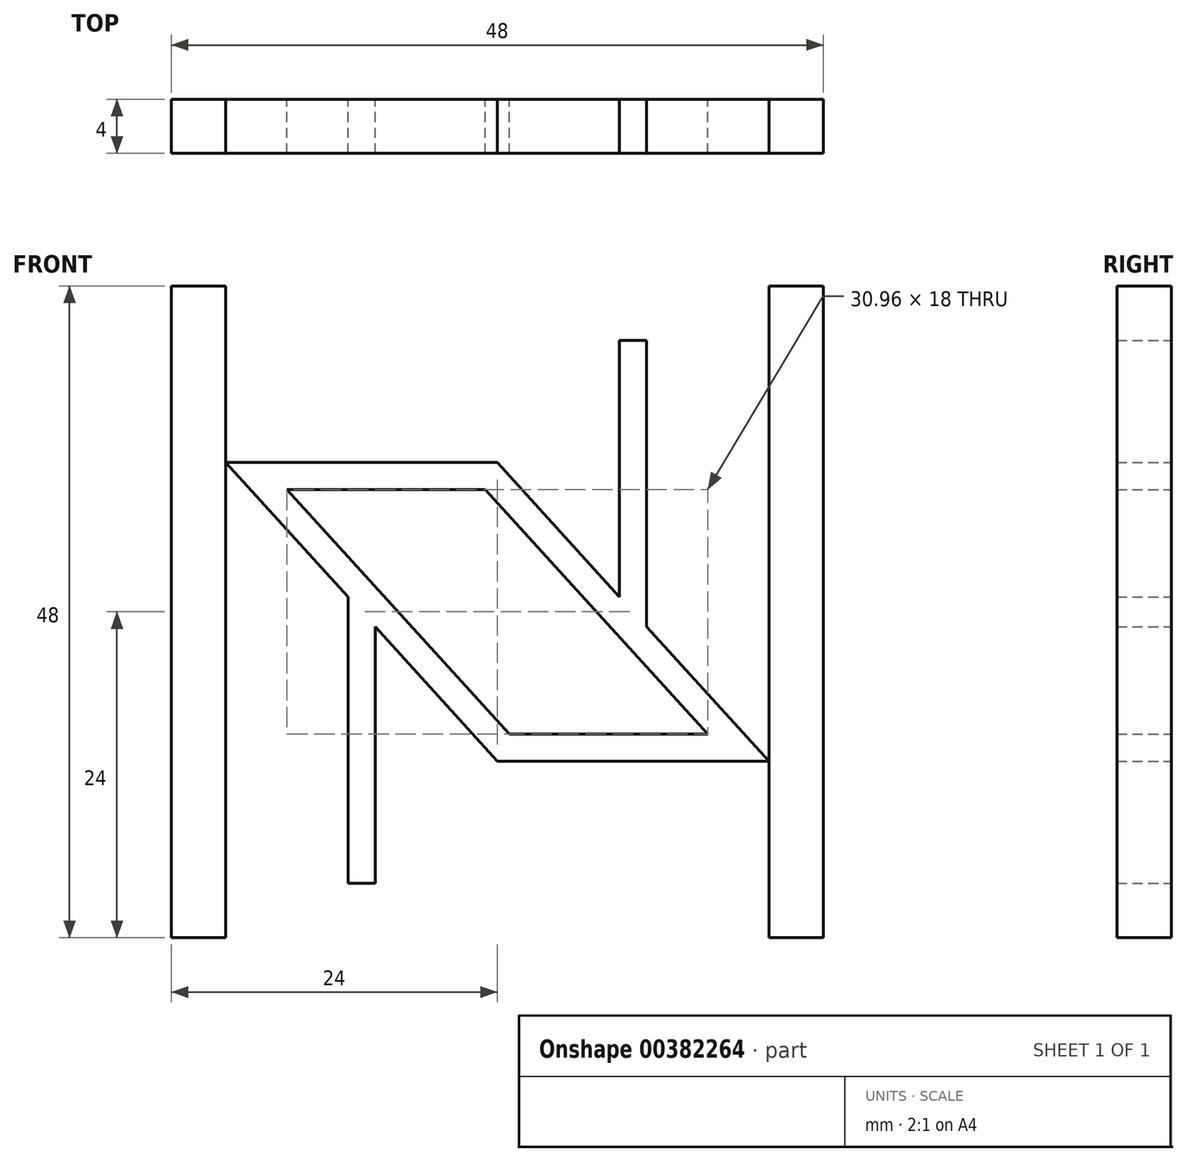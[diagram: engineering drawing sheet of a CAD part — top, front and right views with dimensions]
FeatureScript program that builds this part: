
annotation { "Feature Type Name" : "Feature", "Feature Type Description" : "" }
export const myFeature = defineFeature(function(context is Context, id is Id, definition is map)
    precondition{}
    {
        {
            var Q0;
            Q0=qCreatedBy(makeId("Front.planeOp"),FACE);
            var sketch = newSketch(context, id + "F0", { "sketchPlane" : qUnion([Q0])});
            skPoint(sketch, "E0", {"position": v(0, 0) * mm});
            skPoint(sketch, "E1", {"position": v(0, 20) * mm});
            skPoint(sketch, "E2", {"position": v(20, 0) * mm});
            skPoint(sketch, "E3", {"position": v(-20, 0) * mm});
            skPoint(sketch, "E4", {"position": v(0, -20) * mm});
            skPoint(sketch, "E5", {"position": v(-20, 20) * mm});
            skPoint(sketch, "E6", {"position": v(20, -20) * mm});
            skPoint(sketch, "E7", {"position": v(20, 20) * mm});
            skPoint(sketch, "E8", {"position": v(-20, -20) * mm});
            skPoint(sketch, "E9", {"position": v(-20, 11) * mm});
            skPoint(sketch, "E10", {"position": v(20, -11) * mm});
            skLineSegment(sketch, "E11", {"start": v(-20, 11) * mm, "end": v(0, 11) * mm});
            skLineSegment(sketch, "E12", {"start": v(0, 11) * mm, "end": v(20, -11) * mm});
            skLineSegment(sketch, "E13", {"start": v(20, -11) * mm, "end": v(0, -11) * mm});
            skLineSegment(sketch, "E14", {"start": v(0, -11) * mm, "end": v(-20, 11) * mm});
            skPoint(sketch, "E15", {"position": v(11, 20) * mm});
            skPoint(sketch, "E16", {"position": v(-11, -20) * mm});
            skPoint(sketch, "E17", {"position": v(-9, -20) * mm});
            skPoint(sketch, "E18", {"position": v(9, 20) * mm});
            skLineSegment(sketch, "E19.bottom", {"start": v(-20, 11) * mm, "end": v(1.82, 11) * mm});
            skLineSegment(sketch, "E19.top", {"start": v(-20, 9) * mm, "end": v(1.82, 9) * mm});
            skLineSegment(sketch, "E19.left", {"start": v(-20, 11) * mm, "end": v(-20, 9) * mm});
            skLineSegment(sketch, "E19.right", {"start": v(1.82, 11) * mm, "end": v(1.82, 9) * mm});
            skLineSegment(sketch, "E20.bottom", {"start": v(20, -11) * mm, "end": v(-1.82, -11) * mm});
            skLineSegment(sketch, "E20.top", {"start": v(20, -9) * mm, "end": v(-1.82, -9) * mm});
            skLineSegment(sketch, "E20.left", {"start": v(20, -11) * mm, "end": v(20, -9) * mm});
            skLineSegment(sketch, "E20.right", {"start": v(-1.82, -11) * mm, "end": v(-1.82, -9) * mm});
            skLineSegment(sketch, "E21", {"start": v(-0.88, 9) * mm, "end": v(15.48, -9) * mm});
            skLineSegment(sketch, "E22", {"start": v(-15.48, 9) * mm, "end": v(0.88, -9) * mm});
            skLineSegment(sketch, "E23", {"start": v(11, 20) * mm, "end": v(11, -1.1) * mm});
            skLineSegment(sketch, "E24", {"start": v(9, 20) * mm, "end": v(9, 1.1) * mm});
            skLineSegment(sketch, "E25", {"start": v(-9, -20) * mm, "end": v(-9, -1.1) * mm});
            skLineSegment(sketch, "E26", {"start": v(-11, -20) * mm, "end": v(-11, 1.1) * mm});
            skLineSegment(sketch, "E27.bottom", {"start": v(-20, 20) * mm, "end": v(20, 20) * mm});
            skLineSegment(sketch, "E27.top", {"start": v(-20, 24) * mm, "end": v(20, 24) * mm});
            skLineSegment(sketch, "E27.left", {"start": v(-20, 20) * mm, "end": v(-20, 24) * mm});
            skLineSegment(sketch, "E27.right", {"start": v(20, 20) * mm, "end": v(20, 24) * mm});
            skLineSegment(sketch, "E28.bottom", {"start": v(-20, -20) * mm, "end": v(20, -20) * mm});
            skLineSegment(sketch, "E28.top", {"start": v(-20, -24) * mm, "end": v(20, -24) * mm});
            skLineSegment(sketch, "E28.left", {"start": v(-20, -20) * mm, "end": v(-20, -24) * mm});
            skLineSegment(sketch, "E28.right", {"start": v(20, -20) * mm, "end": v(20, -24) * mm});
            skLineSegment(sketch, "E29.bottom", {"start": v(20, 24) * mm, "end": v(24, 24) * mm});
            skLineSegment(sketch, "E29.top", {"start": v(20, -24) * mm, "end": v(24, -24) * mm});
            skLineSegment(sketch, "E29.left", {"start": v(20, 24) * mm, "end": v(20, -24) * mm});
            skLineSegment(sketch, "E29.right", {"start": v(24, 24) * mm, "end": v(24, -24) * mm});
            skLineSegment(sketch, "E30.bottom", {"start": v(-20, 24) * mm, "end": v(-24, 24) * mm});
            skLineSegment(sketch, "E30.top", {"start": v(-20, -24) * mm, "end": v(-24, -24) * mm});
            skLineSegment(sketch, "E30.left", {"start": v(-20, 24) * mm, "end": v(-20, -24) * mm});
            skLineSegment(sketch, "E30.right", {"start": v(-24, 24) * mm, "end": v(-24, -24) * mm});
            skSolve(sketch);
        }
        {
            var Q0;
            {var subQ0=sQuery(id+"F0.wireOp",EDGE,"E19.top");var subQ1=makeQuery(id+"F0.imprint","INTERSECT",VERTEX,{"derivedFrom":[subQ0,sQuery(id+"F0.wireOp",EDGE,"E22")]});Q0=makeQuery(id+"F0.imprint","IMPRINT",FACE,{"disambiguationData":[TD([[makeQuery(id+"F0.imprint","IMPRINT",EDGE,{"disambiguationData":[TD([[subQ1,1.0]])],"derivedFrom":subQ0}),1.0]])]});}
            var Q1;
            {var subQ0=sQuery(id+"F0.wireOp",EDGE,"E22");Q1=makeQuery(id+"F0.imprint","IMPRINT",FACE,{"disambiguationData":[TD([[makeQuery(id+"F0.imprint","IMPRINT",EDGE,{"derivedFrom":subQ0}),-1.0]])]});}
            var Q2;
            {var subQ3=sQuery(id+"F0.wireOp",EDGE,"E21");Q2=makeQuery(id+"F0.imprint","IMPRINT",FACE,{"disambiguationData":[TD([[makeQuery(id+"F0.imprint","IMPRINT",EDGE,{"derivedFrom":subQ3}),1.0]])]});}
            var Q3;
            {var subQ5=sQuery(id+"F0.wireOp",EDGE,"E20.top");var subQ6=makeQuery(id+"F0.imprint","INTERSECT",VERTEX,{"derivedFrom":[subQ5,sQuery(id+"F0.wireOp",EDGE,"E21")]});Q3=makeQuery(id+"F0.imprint","IMPRINT",FACE,{"disambiguationData":[TD([[makeQuery(id+"F0.imprint","IMPRINT",EDGE,{"disambiguationData":[TD([[subQ6,1.0]])],"derivedFrom":subQ5}),1.0]])]});}
            var Q4;
            {var subQ0=sQuery(id+"F0.wireOp",EDGE,"E23");Q4=makeQuery(id+"F0.imprint","IMPRINT",FACE,{"disambiguationData":[TD([[makeQuery(id+"F0.imprint","IMPRINT",EDGE,{"derivedFrom":subQ0}),-1.0]])]});}
            var Q5;
            {var subQ0=sQuery(id+"F0.wireOp",EDGE,"E25");Q5=makeQuery(id+"F0.imprint","IMPRINT",FACE,{"disambiguationData":[TD([[makeQuery(id+"F0.imprint","IMPRINT",EDGE,{"derivedFrom":subQ0}),1.0]])]});}
            var Q6;
            {var subQ3=sQuery(id+"F0.wireOp",EDGE,"E30.bottom");Q6=makeQuery(id+"F0.imprint","IMPRINT",FACE,{"disambiguationData":[TD([[makeQuery(id+"F0.imprint","IMPRINT",EDGE,{"derivedFrom":subQ3}),1.0]])]});}
            var Q7;
            {var subQ3=sQuery(id+"F0.wireOp",EDGE,"E29.bottom");Q7=makeQuery(id+"F0.imprint","IMPRINT",FACE,{"disambiguationData":[TD([[makeQuery(id+"F0.imprint","IMPRINT",EDGE,{"derivedFrom":subQ3}),-1.0]])]});}
            extrude(context, id + "F1", {"entities" : qUnion([Q0, Q1, Q2, Q3, Q4, Q5, Q6, Q7]), "depth" : 4 * mm});
        }
    });
